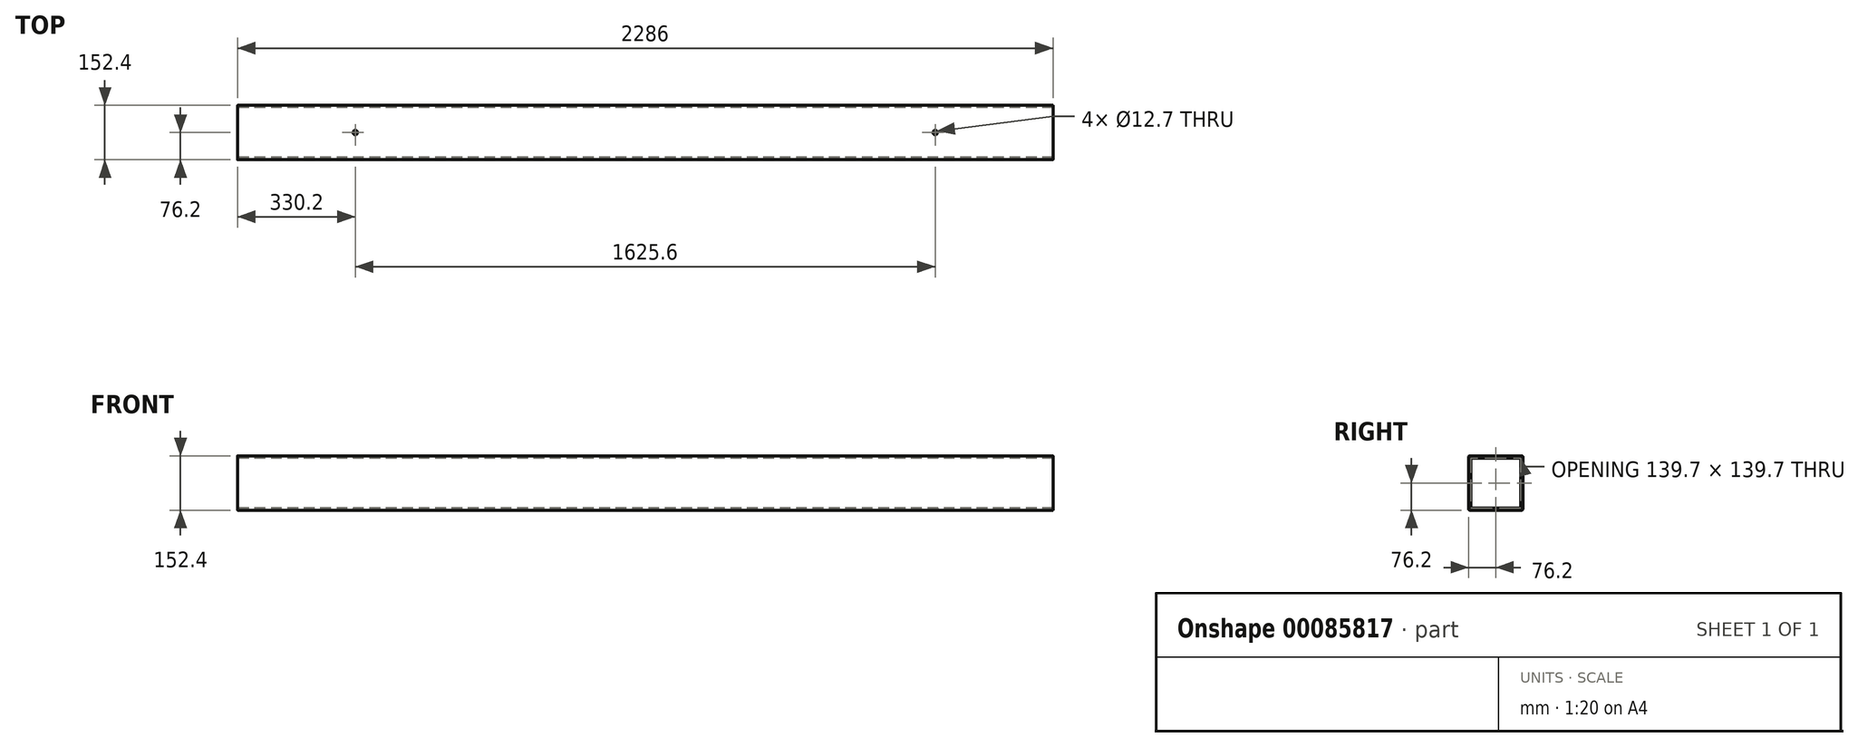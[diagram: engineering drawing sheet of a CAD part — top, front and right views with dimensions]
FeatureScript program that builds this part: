
annotation { "Feature Type Name" : "Feature", "Feature Type Description" : "" }
export const myFeature = defineFeature(function(context is Context, id is Id, definition is map)
    precondition{}
    {
        {
            var Q0;
            Q0=qCreatedBy(makeId("Right.planeOp"),FACE);
            var sketch = newSketch(context, id + "F0", { "sketchPlane" : qUnion([Q0])});
            skLineSegment(sketch, "E0.bottom", {"start": v(-73.03, 76.2) * mm, "end": v(73.03, 76.2) * mm});
            skLineSegment(sketch, "E0.top", {"start": v(-73.03, -76.2) * mm, "end": v(73.02, -76.2) * mm});
            skLineSegment(sketch, "E0.left", {"start": v(-76.2, 73.02) * mm, "end": v(-76.2, -73.03) * mm});
            skLineSegment(sketch, "E0.right", {"start": v(76.2, 73.02) * mm, "end": v(76.2, -73.03) * mm});
            skPoint(sketch, "E0.middle", {"position": v(0, 0) * mm});
            skLineSegment(sketch, "E1.0", {"start": v(-69.85, 66.68) * mm, "end": v(-69.85, -66.67) * mm});
            skLineSegment(sketch, "E2.3", {"start": v(-66.68, -69.85) * mm, "end": v(66.68, -69.85) * mm});
            skLineSegment(sketch, "E3.0", {"start": v(69.85, 66.68) * mm, "end": v(69.85, -66.67) * mm});
            skLineSegment(sketch, "E3.1", {"start": v(-66.68, 69.85) * mm, "end": v(66.68, 69.85) * mm});
            skPoint(sketch, "E4.visualSharp", {"position": v(-76.2, 76.2) * mm});
            skArc(sketch, "E4.filletArc", {"start": v(-73.03, 76.2) * mm, "mid": v(-75.27, 75.27) * mm, "end": v(-76.2, 73.02) * mm});
            skPoint(sketch, "E5.visualSharp", {"position": v(76.2, 76.2) * mm});
            skArc(sketch, "E5.filletArc", {"start": v(76.2, 73.02) * mm, "mid": v(75.27, 75.27) * mm, "end": v(73.03, 76.2) * mm});
            skPoint(sketch, "E6.visualSharp", {"position": v(76.2, -76.2) * mm});
            skArc(sketch, "E6.filletArc", {"start": v(73.02, -76.2) * mm, "mid": v(75.27, -75.27) * mm, "end": v(76.2, -73.03) * mm});
            skPoint(sketch, "E7.visualSharp", {"position": v(-76.2, -76.2) * mm});
            skArc(sketch, "E7.filletArc", {"start": v(-76.2, -73.03) * mm, "mid": v(-75.27, -75.27) * mm, "end": v(-73.03, -76.2) * mm});
            skPoint(sketch, "E8.visualSharp", {"position": v(-69.85, -69.85) * mm});
            skArc(sketch, "E8.filletArc", {"start": v(-69.85, -66.67) * mm, "mid": v(-68.92, -68.92) * mm, "end": v(-66.68, -69.85) * mm});
            skPoint(sketch, "E9.visualSharp", {"position": v(-69.85, 69.85) * mm});
            skArc(sketch, "E9.filletArc", {"start": v(-66.68, 69.85) * mm, "mid": v(-68.92, 68.92) * mm, "end": v(-69.85, 66.68) * mm});
            skPoint(sketch, "E10.visualSharp", {"position": v(69.85, 69.85) * mm});
            skArc(sketch, "E10.filletArc", {"start": v(69.85, 66.68) * mm, "mid": v(68.92, 68.92) * mm, "end": v(66.68, 69.85) * mm});
            skPoint(sketch, "E11.visualSharp", {"position": v(69.85, -69.85) * mm});
            skArc(sketch, "E11.filletArc", {"start": v(66.68, -69.85) * mm, "mid": v(68.92, -68.92) * mm, "end": v(69.85, -66.67) * mm});
            skSolve(sketch);
        }
        {
            var Q0;
            Q0=makeQuery(id+"F0.imprint","IMPRINT",FACE,{"disambiguationData":[TD([[makeQuery(id+"F0.imprint","IMPRINT",EDGE,{"derivedFrom":sQuery(id+"F0.wireOp",EDGE,"E0.bottom")}),-1.0]])]});
            extrude(context, id + "F1", {"entities" : qUnion([Q0]), "depth" : 2286 * mm, "hasSecondDirection" : true, "secondDirectionOppositeDirection" : true, "secondDirectionDepth" : 0 * mm, "offsetDistance" : 25.4 * mm});
        }
        {
            var Q0;
            Q0=makeQuery(id+"F1.opExtrude","SWEPT_FACE",FACE,{"disambiguationData":[OSD([sQuery(id+"F0.wireOp",EDGE,"E0.top")])]});
            var sketch = newSketch(context, id + "F2", { "sketchPlane" : qUnion([Q0])});
            skPoint(sketch, "E12", {"position": v(1955.8, 0) * mm});
            skPoint(sketch, "E12.positionSnap0", {"position": v(2286, 0) * mm});
            skPoint(sketch, "E13", {"position": v(330.2, 0) * mm});
            skPoint(sketch, "E13.positionSnap0", {"position": v(0, 0) * mm});
            skCircle(sketch, "E14", {"center": v(330.2, 0) * mm, "radius": 6.35 * mm});
            skCircle(sketch, "E15", {"center": v(1955.8, 0) * mm, "radius": 6.35 * mm});
            skSolve(sketch);
        }
        {
            var Q0;
            Q0=makeQuery(id+"F2.imprint","IMPRINT",FACE,{"disambiguationData":[TD([[makeQuery(id+"F2.imprint","IMPRINT",EDGE,{"derivedFrom":sQuery(id+"F2.wireOp",EDGE,"E14")}),1.0]])]});
            var Q1;
            Q1=makeQuery(id+"F2.imprint","IMPRINT",FACE,{"disambiguationData":[TD([[makeQuery(id+"F2.imprint","IMPRINT",EDGE,{"derivedFrom":sQuery(id+"F2.wireOp",EDGE,"E15")}),1.0]])]});
            extrude(context, id + "F3", {"entities" : qUnion([Q0, Q1]), "operationType" : NewBodyOperationType.REMOVE, "endBound" : BoundingType.THROUGH_ALL, "oppositeDirection" : true, "depth" : 152.4 * mm, "offsetDistance" : 25.4 * mm});
        }
    });
